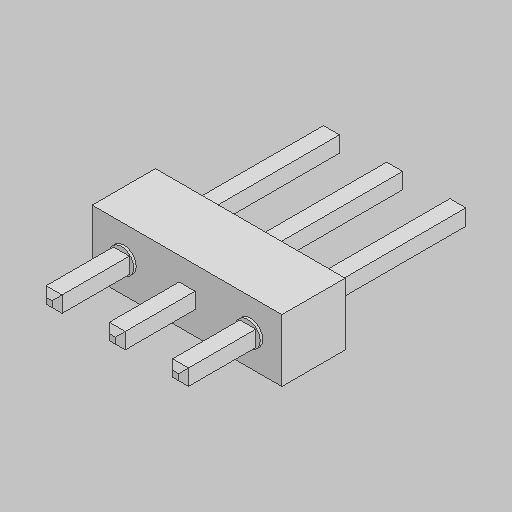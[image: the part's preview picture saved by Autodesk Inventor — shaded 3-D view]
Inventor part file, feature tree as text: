
AUTODESK INVENTOR PART (.ipt)
format: ipt  version: 2023.5 (Build 275446000, 446)  size: 189,440 bytes
history: native  units: mm
features: extrude x4, projected_geometry x3, chamfer x1
ambient origin geometry x8: Origin, YZ Plane, XZ Plane, XY Plane, X Axis, Y Axis, Z Axis, Center Point
bodies: Solid1 (feature_tree)
feature tree (8):
  extrude  "Extrusion1"  Depth=7.62mm
  extrude  "Extrusion2"  Depth=2.5mm
  extrude  "Extrusion3"  Depth=2.54mm TaperAngle=0.0deg
  chamfer  "Chamfer1"  Distance=0.64mm
  extrude  "Extrusion4"  Depth=0.64mm
  projected_geometry  "Projected Loop1"
  projected_geometry  "Projected Loop2"
  projected_geometry  "Projected Loop3"
